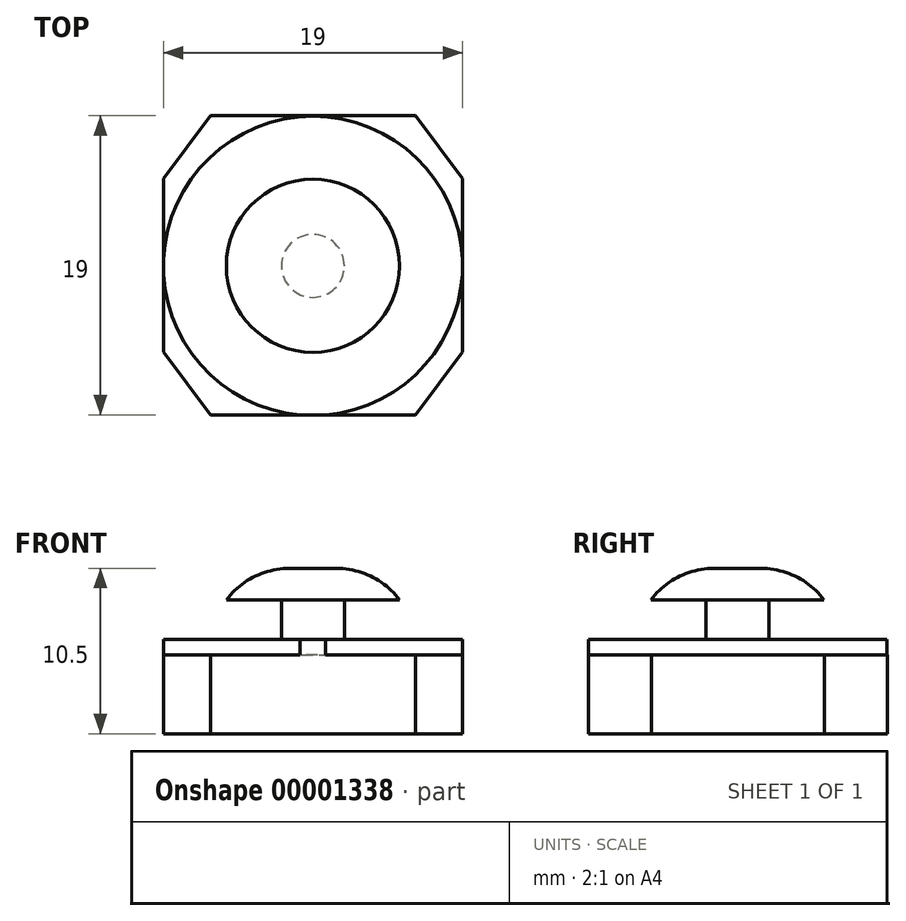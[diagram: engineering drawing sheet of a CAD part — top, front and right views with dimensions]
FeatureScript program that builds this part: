
annotation { "Feature Type Name" : "Feature", "Feature Type Description" : "" }
export const myFeature = defineFeature(function(context is Context, id is Id, definition is map)
    precondition{}
    {
        {
            var Q0;
            Q0=qCreatedBy(makeId("Top.planeOp"),FACE);
            var sketch = newSketch(context, id + "F0", { "sketchPlane" : qUnion([Q0])});
            skLineSegment(sketch, "E0", {"start": v(0, 0) * mm, "end": v(-3, 4) * mm});
            skLineSegment(sketch, "E1", {"start": v(-3, 4) * mm, "end": v(-3, 15) * mm});
            skLineSegment(sketch, "E2", {"start": v(-3, 15) * mm, "end": v(0, 19) * mm});
            skLineSegment(sketch, "E3", {"start": v(0, 19) * mm, "end": v(13, 19) * mm});
            skLineSegment(sketch, "E4", {"start": v(13, 19) * mm, "end": v(16, 15) * mm});
            skLineSegment(sketch, "E5", {"start": v(16, 15) * mm, "end": v(16, 4) * mm});
            skLineSegment(sketch, "E6", {"start": v(16, 4) * mm, "end": v(13, 0) * mm});
            skLineSegment(sketch, "E7", {"start": v(13, 0) * mm, "end": v(0, 0) * mm});
            skSolve(sketch);
        }
        {
            var Q0;
            Q0=makeQuery(id+"F0.imprint","IMPRINT",FACE,{"disambiguationData":[TD([[makeQuery(id+"F0.imprint","IMPRINT",EDGE,{"derivedFrom":sQuery(id+"F0.wireOp",EDGE,"E0")}),-1.0]])]});
            extrude(context, id + "F1", {"entities" : qUnion([Q0]), "depth" : 5 * mm});
        }
        {
            var Q0;
            Q0=makeQuery(id+"F1.opExtrude","CAP_FACE",FACE,{"disambiguationData":[OSD([sQuery(id+"F0.wireOp",EDGE,"E0"),sQuery(id+"F0.wireOp",EDGE,"E1"),sQuery(id+"F0.wireOp",EDGE,"E2"),sQuery(id+"F0.wireOp",EDGE,"E3"),sQuery(id+"F0.wireOp",EDGE,"E4"),sQuery(id+"F0.wireOp",EDGE,"E5"),sQuery(id+"F0.wireOp",EDGE,"E6"),sQuery(id+"F0.wireOp",EDGE,"E7")])],"isStart":false});
            var sketch = newSketch(context, id + "F2", { "sketchPlane" : qUnion([Q0])});
            skCircle(sketch, "E8", {"center": v(6.5, 9.47) * mm, "radius": 9.5 * mm});
            skSolve(sketch);
        }
        {
            var Q0;
            {var subQ1=sQuery(id+"F2.wireOp",EDGE,"E8");var subQ5=makeQuery(id+"F2.imprint","INTERSECT",VERTEX,{"derivedFrom":[makeQuery(id+"F1.opExtrude","CAP_EDGE",EDGE,{"disambiguationData":[OSD([sQuery(id+"F0.wireOp",EDGE,"E1")])],"isStart":false}),subQ1]});Q0=makeQuery(id+"F2.imprint","IMPRINT",FACE,{"disambiguationData":[TD([[makeQuery(id+"F2.imprint","IMPRINT",EDGE,{"disambiguationData":[TD([[subQ5,1.0]])],"derivedFrom":subQ1}),1.0]])]});}
            extrude(context, id + "F3", {"entities" : qUnion([Q0]), "operationType" : NewBodyOperationType.ADD, "depth" : 1 * mm});
        }
        {
            var Q0;
            Q0=makeQuery(id+"F3.opExtrude","CAP_FACE",FACE,{"disambiguationData":[OSD([sQuery(id+"F0.wireOp",EDGE,"E7"),sQuery(id+"F2.wireOp",EDGE,"E8")])],"isStart":false});
            var sketch = newSketch(context, id + "F4", { "sketchPlane" : qUnion([Q0])});
            skArc(sketch, "E9.0", {"start": v(7.3, 0) * mm, "mid": v(6.5, 18.97) * mm, "end": v(5.7, 0) * mm});
            skCircle(sketch, "E10", {"center": v(6.5, 9.47) * mm, "radius": 2 * mm});
            skSolve(sketch);
        }
        {
            var Q0;
            Q0=makeQuery(id+"F4.imprint","IMPRINT",FACE,{"disambiguationData":[TD([[makeQuery(id+"F4.imprint","IMPRINT",EDGE,{"derivedFrom":sQuery(id+"F4.wireOp",EDGE,"E10")}),1.0]])]});
            extrude(context, id + "F5", {"entities" : qUnion([Q0]), "operationType" : NewBodyOperationType.ADD, "depth" : 2.5 * mm});
        }
        {
            var Q0;
            Q0=makeQuery(id+"F5.opExtrude","CAP_FACE",FACE,{"disambiguationData":[OSD([sQuery(id+"F4.wireOp",EDGE,"E10")])],"isStart":false});
            var sketch = newSketch(context, id + "F6", { "sketchPlane" : qUnion([Q0])});
            skCircle(sketch, "E11.0", {"center": v(6.5, 9.47) * mm, "radius": 2 * mm});
            skCircle(sketch, "E12", {"center": v(6.5, 9.47) * mm, "radius": 5.5 * mm});
            skSolve(sketch);
        }
        {
            var Q0;
            Q0=makeQuery(id+"F6.imprint","IMPRINT",FACE,{"disambiguationData":[TD([[makeQuery(id+"F6.imprint","IMPRINT",EDGE,{"derivedFrom":sQuery(id+"F6.wireOp",EDGE,"E11.0")}),-1.0]])]});
            var Q1;
            Q1=makeQuery(id+"F6.imprint","IMPRINT",FACE,{"disambiguationData":[TD([[makeQuery(id+"F6.imprint","IMPRINT",EDGE,{"derivedFrom":sQuery(id+"F6.wireOp",EDGE,"E11.0")}),1.0]])]});
            extrude(context, id + "F7", {"entities" : qUnion([Q0, Q1]), "operationType" : NewBodyOperationType.ADD, "depth" : 2 * mm});
        }
        {
            var Q0;
            Q0=makeQuery(id+"F7.opExtrude","CAP_EDGE",EDGE,{"disambiguationData":[OSD([sQuery(id+"F6.wireOp",EDGE,"E12")])],"isStart":false});
            fillet(context, id + "F8", {"entities" : qUnion([Q0]), "radius" : 5 * mm, "tangentPropagation" : true, "allowEdgeOverflow" : false});
        }
    });
